# Revit family: Switch-Lutron-EcoSystem_CC-4BRL
name_source: partatom
category: Lighting Devices
revit_build: Autodesk Revit 2017 (Build: 20160720_1515(x64)
units: mm (PartAtom-declared; Revit-internal decimal feet)

## family parameters
Cut with Voids When Loaded = No
Host = Face
Maintain Annotation Orientation = Yes
OmniClass Number = 23.85.80.11.27
OmniClass Title = Lighting Controls
Part Type = Switch
Room Calculation Point = No
Round Connector Dimension = Use Diameter
Shared = No

## types (2) — shared parameters
Assembly Code = D5020120
Default Elevation = 4' - 0"
Description = 4 Button Wall Control
Instruction Sheet Link = http://www.lutron.com
Manufacturer = Lutron Electronics Co., Inc
Manufacturer Fax Number = 610-282-1243
Nominal Depth = 0' - 1 3/4"
Nominal Height = 0' - 4 11/16"
Nominal Width = 0' - 2 15/16"
Performance URL = http://www.lutron.com
Product Documentation Link = http://www.lutron.com
Product Name = 4 Button Wall Control
Product Page URL = http://www.lutron.com
Series = EcoSystem
URL = http://www.lutron.com
Version = 2017 - v1.0b
Video Link = https://www.youtube.com
Voltage Comments = 0-20VDC
Warranty URL = http://www.lutron.com
zero-valued in all types: Cost

## per-type parameters (varying)
| type | Wallstation Material |
| CC-4BRL-WH | Plastic-Lutron-Claro-White-Gloss |
| CC-4BRL-IV | Plastic-Lutron-Claro-Ivory-Gloss |

note: column(s) folded — value = type name in every type: Model

## geometry (parser evidence)
native form markers: Sweep x3
no freeform markers — native parametric forms only
